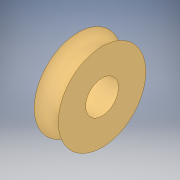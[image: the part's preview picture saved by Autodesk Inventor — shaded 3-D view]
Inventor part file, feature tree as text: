
AUTODESK INVENTOR PART (.ipt)
format: ipt  version: 2019 (Build 230136000, 136)  size: 133,120 bytes
history: imported  units: in
note: dims shown in document units (in); Inventor stores cm internally (conversion verified against a paired STEP export)
features: imported_body x1
ambient origin geometry x8: Origin, YZ Plane, XZ Plane, XY Plane, X Axis, Y Axis, Z Axis, Center Point
bodies: Solid1 (imported_parasolid), Body1 (imported_parasolid)
feature tree (1):
  imported_body  NMx_Import_Brep_tag  [imported B-rep: ~4 faces, bbox_mm=[2.2, 0.0, 2.5]]
